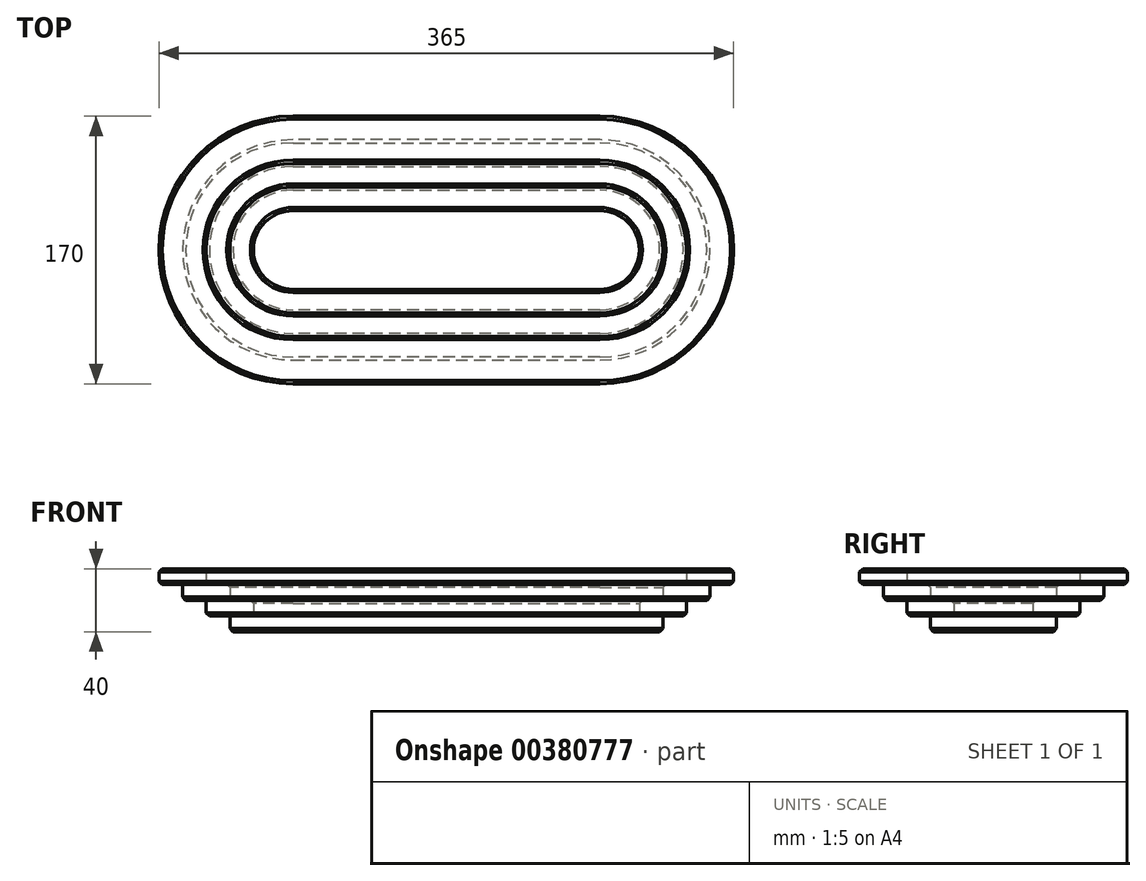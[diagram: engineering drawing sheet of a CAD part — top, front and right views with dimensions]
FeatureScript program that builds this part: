
annotation { "Feature Type Name" : "Feature", "Feature Type Description" : "" }
export const myFeature = defineFeature(function(context is Context, id is Id, definition is map)
    precondition{}
    {
        {
            var Q0;
            Q0=qCreatedBy(makeId("Top.planeOp"),FACE);
            var sketch = newSketch(context, id + "F0", { "sketchPlane" : qUnion([Q0])});
            skLineSegment(sketch, "E0", {"start": v(-97.5, 0) * mm, "end": v(97.5, 0) * mm, "construction": true});
            skArc(sketch, "E1", {"start": v(-97.5, 40) * mm, "mid": v(-137.5, 0) * mm, "end": v(-97.5, -40) * mm});
            skArc(sketch, "E2", {"start": v(97.5, -40) * mm, "mid": v(137.5, 0) * mm, "end": v(97.5, 40) * mm});
            skLineSegment(sketch, "E3", {"start": v(-97.5, 40) * mm, "end": v(97.5, 40) * mm});
            skLineSegment(sketch, "E4", {"start": v(-97.5, -40) * mm, "end": v(97.5, -40) * mm});
            skPoint(sketch, "E5", {"position": v(137.5, 0) * mm});
            skSolve(sketch);
        }
        {
            var Q0;
            Q0 = qSketchRegion(id + "F0", true);
            extrude(context, id + "F1", {"entities" : qUnion([Q0]), "depth" : 10 * mm});
        }
        {
            var Q0;
            Q0=makeQuery(id+"F1.opExtrude","CAP_FACE",FACE,{"disambiguationData":[OSD([sQuery(id+"F0.wireOp",EDGE,"E1"),sQuery(id+"F0.wireOp",EDGE,"E2"),sQuery(id+"F0.wireOp",EDGE,"E3"),sQuery(id+"F0.wireOp",EDGE,"E4")])],"isStart":false});
            var sketch = newSketch(context, id + "F2", { "sketchPlane" : qUnion([Q0])});
            skArc(sketch, "E6.0", {"start": v(-97.5, 40) * mm, "mid": v(-137.5, 0) * mm, "end": v(-97.5, -40) * mm});
            skLineSegment(sketch, "E6.1", {"start": v(-97.5, 40) * mm, "end": v(97.5, 40) * mm});
            skArc(sketch, "E6.2", {"start": v(97.5, -40) * mm, "mid": v(137.5, 0) * mm, "end": v(97.5, 40) * mm});
            skLineSegment(sketch, "E6.3", {"start": v(-97.5, -40) * mm, "end": v(97.5, -40) * mm});
            skLineSegment(sketch, "E7.0", {"start": v(-97.5, -55) * mm, "end": v(97.5, -55) * mm});
            skArc(sketch, "E7.1", {"start": v(-97.5, 55) * mm, "mid": v(-152.5, 0) * mm, "end": v(-97.5, -55) * mm});
            skLineSegment(sketch, "E7.2", {"start": v(-97.5, 55) * mm, "end": v(97.5, 55) * mm});
            skArc(sketch, "E7.3", {"start": v(97.5, -55) * mm, "mid": v(152.5, 0) * mm, "end": v(97.5, 55) * mm});
            skLineSegment(sketch, "E8.0", {"start": v(-97.5, -25) * mm, "end": v(97.5, -25) * mm});
            skArc(sketch, "E8.1", {"start": v(-97.5, 25) * mm, "mid": v(-122.5, 0) * mm, "end": v(-97.5, -25) * mm});
            skLineSegment(sketch, "E8.2", {"start": v(-97.5, 25) * mm, "end": v(97.5, 25) * mm});
            skArc(sketch, "E8.3", {"start": v(97.5, -25) * mm, "mid": v(122.5, 0) * mm, "end": v(97.5, 25) * mm});
            skSolve(sketch);
        }
        {
            var Q0;
            Q0 = qSketchRegion(id + "F2", true);
            var Q1;
            Q1=makeQuery(id+"F2.imprint","IMPRINT",FACE,{"disambiguationData":[TD([[makeQuery(id+"F2.imprint","IMPRINT",EDGE,{"derivedFrom":sQuery(id+"F2.wireOp",EDGE,"E6.0")}),1.0]])]});
            extrude(context, id + "F3", {"entities" : qUnion([Q0, Q1]), "depth" : 10 * mm});
        }
        {
            var Q0;
            Q0=makeQuery(id+"F3.opExtrude","CAP_FACE",FACE,{"disambiguationData":[OSD([sQuery(id+"F2.wireOp",EDGE,"E7.0"),sQuery(id+"F2.wireOp",EDGE,"E7.1"),sQuery(id+"F2.wireOp",EDGE,"E7.2"),sQuery(id+"F2.wireOp",EDGE,"E7.3"),sQuery(id+"F2.wireOp",EDGE,"E8.0"),sQuery(id+"F2.wireOp",EDGE,"E8.1"),sQuery(id+"F2.wireOp",EDGE,"E8.2"),sQuery(id+"F2.wireOp",EDGE,"E8.3")])],"isStart":false});
            var sketch = newSketch(context, id + "F4", { "sketchPlane" : qUnion([Q0])});
            skLineSegment(sketch, "E9.0", {"start": v(-97.5, 55) * mm, "end": v(97.5, 55) * mm});
            skArc(sketch, "E9.1", {"start": v(97.5, -55) * mm, "mid": v(152.5, 0) * mm, "end": v(97.5, 55) * mm});
            skLineSegment(sketch, "E9.2", {"start": v(-97.5, -55) * mm, "end": v(97.5, -55) * mm});
            skArc(sketch, "E9.3", {"start": v(-97.5, 55) * mm, "mid": v(-152.5, 0) * mm, "end": v(-97.5, -55) * mm});
            skArc(sketch, "E10.0", {"start": v(-97.5, 70) * mm, "mid": v(-167.5, 0) * mm, "end": v(-97.5, -70) * mm});
            skLineSegment(sketch, "E10.1", {"start": v(-97.5, 70) * mm, "end": v(97.5, 70) * mm});
            skArc(sketch, "E10.2", {"start": v(97.5, -70) * mm, "mid": v(167.5, 0) * mm, "end": v(97.5, 70) * mm});
            skLineSegment(sketch, "E10.3", {"start": v(-97.5, -70) * mm, "end": v(97.5, -70) * mm});
            skArc(sketch, "E11.0", {"start": v(-97.5, 40) * mm, "mid": v(-137.5, 0) * mm, "end": v(-97.5, -40) * mm});
            skLineSegment(sketch, "E11.1", {"start": v(-97.5, 40) * mm, "end": v(97.5, 40) * mm});
            skArc(sketch, "E11.2", {"start": v(97.5, -40) * mm, "mid": v(137.5, 0) * mm, "end": v(97.5, 40) * mm});
            skLineSegment(sketch, "E11.3", {"start": v(-97.5, -40) * mm, "end": v(97.5, -40) * mm});
            skSolve(sketch);
        }
        {
            var Q0;
            Q0 = qSketchRegion(id + "F4", true);
            var Q1;
            Q1=makeQuery(id+"F4.imprint","IMPRINT",FACE,{"disambiguationData":[TD([[makeQuery(id+"F4.imprint","IMPRINT",EDGE,{"derivedFrom":sQuery(id+"F4.wireOp",EDGE,"E9.0")}),-1.0]])]});
            extrude(context, id + "F5", {"entities" : qUnion([Q0, Q1]), "depth" : 10 * mm});
        }
        {
            var Q0;
            Q0=makeQuery(id+"F5.opExtrude","CAP_FACE",FACE,{"disambiguationData":[OSD([sQuery(id+"F4.wireOp",EDGE,"E10.0"),sQuery(id+"F4.wireOp",EDGE,"E10.1"),sQuery(id+"F4.wireOp",EDGE,"E10.2"),sQuery(id+"F4.wireOp",EDGE,"E10.3"),sQuery(id+"F4.wireOp",EDGE,"E11.0"),sQuery(id+"F4.wireOp",EDGE,"E11.1"),sQuery(id+"F4.wireOp",EDGE,"E11.2"),sQuery(id+"F4.wireOp",EDGE,"E11.3")])],"isStart":false});
            var sketch = newSketch(context, id + "F6", { "sketchPlane" : qUnion([Q0])});
            skLineSegment(sketch, "E12.0", {"start": v(-97.5, -70) * mm, "end": v(97.5, -70) * mm});
            skArc(sketch, "E12.1", {"start": v(-97.5, 70) * mm, "mid": v(-167.5, 0) * mm, "end": v(-97.5, -70) * mm});
            skLineSegment(sketch, "E12.2", {"start": v(-97.5, 70) * mm, "end": v(97.5, 70) * mm});
            skArc(sketch, "E12.3", {"start": v(97.5, -70) * mm, "mid": v(167.5, 0) * mm, "end": v(97.5, 70) * mm});
            skLineSegment(sketch, "E13.0", {"start": v(-97.5, -85) * mm, "end": v(97.5, -85) * mm});
            skArc(sketch, "E13.1", {"start": v(-97.5, 85) * mm, "mid": v(-182.5, 0) * mm, "end": v(-97.5, -85) * mm});
            skLineSegment(sketch, "E13.2", {"start": v(-97.5, 85) * mm, "end": v(97.5, 85) * mm});
            skArc(sketch, "E13.3", {"start": v(97.5, -85) * mm, "mid": v(182.5, 0) * mm, "end": v(97.5, 85) * mm});
            skArc(sketch, "E14.0", {"start": v(97.5, -55) * mm, "mid": v(152.5, 0) * mm, "end": v(97.5, 55) * mm});
            skLineSegment(sketch, "E14.1", {"start": v(-97.5, -55) * mm, "end": v(97.5, -55) * mm});
            skArc(sketch, "E14.2", {"start": v(-97.5, 55) * mm, "mid": v(-152.5, 0) * mm, "end": v(-97.5, -55) * mm});
            skLineSegment(sketch, "E14.3", {"start": v(-97.5, 55) * mm, "end": v(97.5, 55) * mm});
            skSolve(sketch);
        }
        {
            var Q0;
            Q0 = qSketchRegion(id + "F6", true);
            var Q1;
            Q1=makeQuery(id+"F6.imprint","IMPRINT",FACE,{"disambiguationData":[TD([[makeQuery(id+"F6.imprint","IMPRINT",EDGE,{"derivedFrom":sQuery(id+"F6.wireOp",EDGE,"E12.0")}),1.0]])]});
            extrude(context, id + "F7", {"entities" : qUnion([Q0, Q1]), "depth" : 10 * mm});
        }
        {
            var Q0;
            Q0=makeQuery(id+"F3.opExtrude","CAP_EDGE",EDGE,{"disambiguationData":[OSD([sQuery(id+"F2.wireOp",EDGE,"E8.0")])],"isStart":false});
            var Q1;
            Q1=makeQuery(id+"F5.opExtrude","CAP_EDGE",EDGE,{"disambiguationData":[OSD([sQuery(id+"F4.wireOp",EDGE,"E11.3")])],"isStart":false});
            var Q2;
            Q2=makeQuery(id+"F7.opExtrude","CAP_EDGE",EDGE,{"disambiguationData":[OSD([sQuery(id+"F6.wireOp",EDGE,"E14.1")])],"isStart":false});
            var Q3;
            Q3=makeQuery(id+"F7.opExtrude","CAP_EDGE",EDGE,{"disambiguationData":[OSD([sQuery(id+"F6.wireOp",EDGE,"E13.2")])],"isStart":false});
            var Q4;
            Q4=makeQuery(id+"F5.opExtrude","CAP_EDGE",EDGE,{"disambiguationData":[OSD([sQuery(id+"F4.wireOp",EDGE,"E10.1")])],"isStart":true});
            var Q5;
            Q5=makeQuery(id+"F3.opExtrude","CAP_EDGE",EDGE,{"disambiguationData":[OSD([sQuery(id+"F2.wireOp",EDGE,"E7.2")])],"isStart":true});
            var Q6;
            Q6=makeQuery(id+"F1.opExtrude","CAP_EDGE",EDGE,{"disambiguationData":[OSD([sQuery(id+"F0.wireOp",EDGE,"E3")])],"isStart":true});
            var Q7;
            Q7=makeQuery(id+"F7.opExtrude","CAP_EDGE",EDGE,{"disambiguationData":[OSD([sQuery(id+"F6.wireOp",EDGE,"E13.1")])],"isStart":true});
            chamfer(context, id + "F8", {"entities" : qUnion([Q0, Q1, Q2, Q3, Q4, Q5, Q6, Q7]), "width" : 2 * mm, "tangentPropagation" : true});
        }
    });
